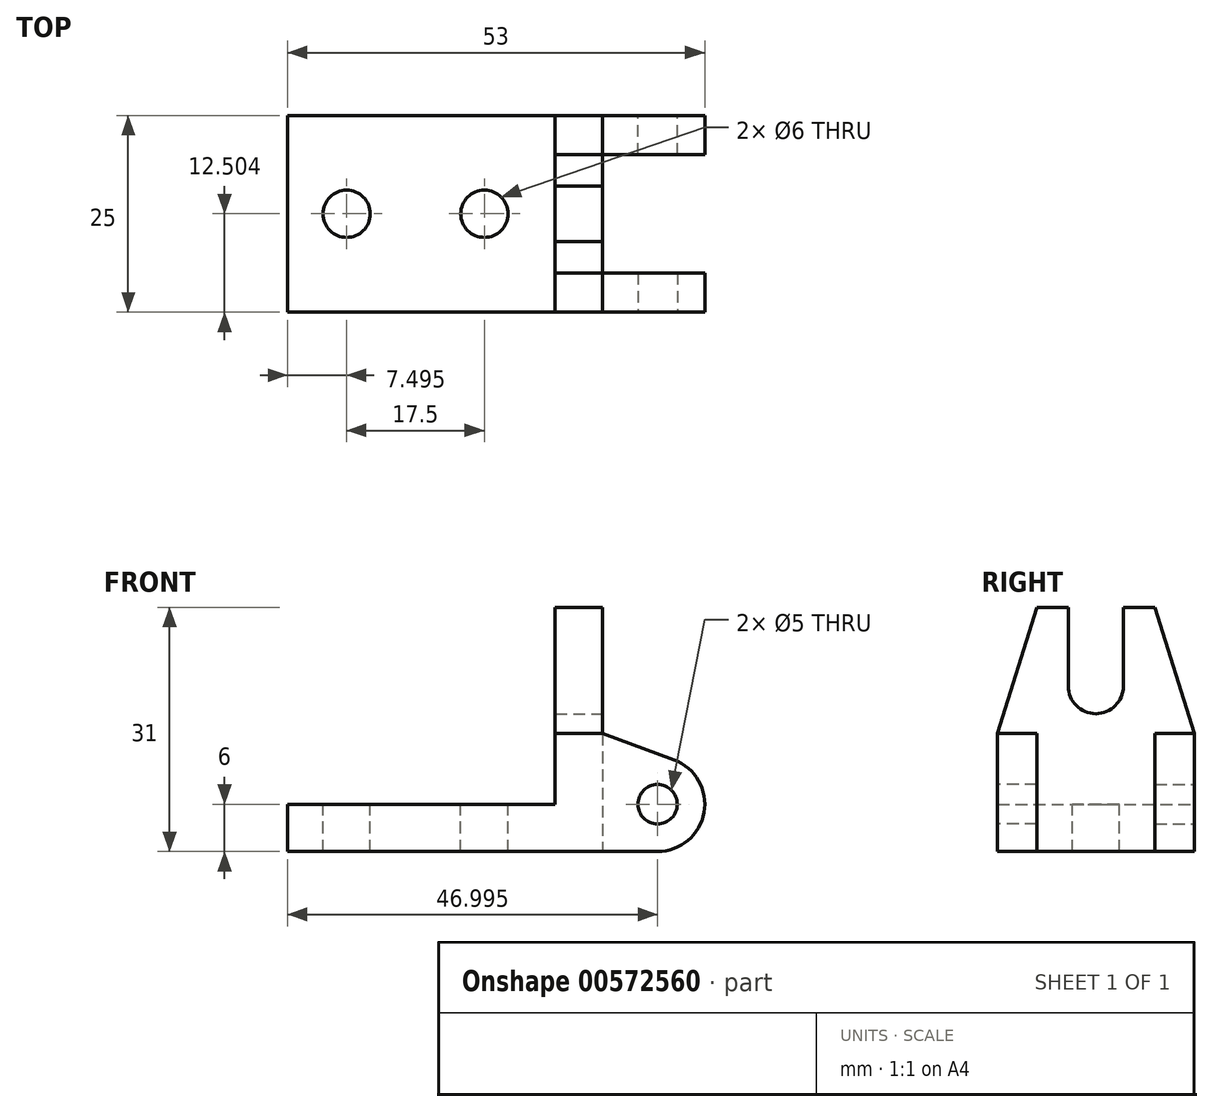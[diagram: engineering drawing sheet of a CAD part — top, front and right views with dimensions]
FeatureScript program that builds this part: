
annotation { "Feature Type Name" : "Feature", "Feature Type Description" : "" }
export const myFeature = defineFeature(function(context is Context, id is Id, definition is map)
    precondition{}
    {
        {
            var Q0;
            Q0=qCreatedBy(makeId("Top.planeOp"),FACE);
            var sketch = newSketch(context, id + "F0", { "sketchPlane" : qUnion([Q0])});
            skLineSegment(sketch, "E0.bottom", {"start": v(-32.98, -3.23) * mm, "end": v(7.02, -3.23) * mm});
            skLineSegment(sketch, "E0.top", {"start": v(-32.98, 21.77) * mm, "end": v(7.02, 21.77) * mm});
            skLineSegment(sketch, "E0.left", {"start": v(-32.98, -3.23) * mm, "end": v(-32.98, 21.77) * mm});
            skLineSegment(sketch, "E0.right", {"start": v(7.02, -3.23) * mm, "end": v(7.02, 21.77) * mm});
            skSolve(sketch);
        }
        {
            var Q0;
            Q0=makeQuery(id+"F0.imprint","IMPRINT",FACE,{"disambiguationData":[TD([[makeQuery(id+"F0.imprint","IMPRINT",EDGE,{"derivedFrom":sQuery(id+"F0.wireOp",EDGE,"E0.bottom")}),1.0]])]});
            extrude(context, id + "F1", {"entities" : qUnion([Q0]), "depth" : 6 * mm, "offsetDistance" : 25 * mm});
        }
        {
            var Q0;
            Q0=makeQuery(id+"F1.opExtrude","CAP_FACE",FACE,{"disambiguationData":[OSD([sQuery(id+"F0.wireOp",EDGE,"E0.bottom"),sQuery(id+"F0.wireOp",EDGE,"E0.top"),sQuery(id+"F0.wireOp",EDGE,"E0.left"),sQuery(id+"F0.wireOp",EDGE,"E0.right")])],"isStart":false});
            var sketch = newSketch(context, id + "F2", { "sketchPlane" : qUnion([Q0])});
            skLineSegment(sketch, "E1.bottom", {"start": v(7.02, -3.23) * mm, "end": v(1.02, -3.23) * mm});
            skLineSegment(sketch, "E1.top", {"start": v(7.02, 21.77) * mm, "end": v(1.02, 21.77) * mm});
            skLineSegment(sketch, "E1.left", {"start": v(7.02, -3.23) * mm, "end": v(7.02, 21.77) * mm});
            skLineSegment(sketch, "E1.right", {"start": v(1.02, -3.23) * mm, "end": v(1.02, 21.77) * mm});
            skSolve(sketch);
        }
        {
            var Q0;
            Q0=makeQuery(id+"F2.imprint","IMPRINT",FACE,{"disambiguationData":[TD([[makeQuery(id+"F2.imprint","IMPRINT",EDGE,{"derivedFrom":sQuery(id+"F2.wireOp",EDGE,"E1.bottom")}),1.0]])]});
            extrude(context, id + "F3", {"entities" : qUnion([Q0]), "operationType" : NewBodyOperationType.ADD, "depth" : 9 * mm, "offsetDistance" : 25 * mm});
        }
        {
            var Q0;
            Q0=makeQuery(id+"F3.boolean.opBoolean","MERGE",FACE,{"derivedFrom":[makeQuery(id+"F1.opExtrude","SWEPT_FACE",FACE,{"disambiguationData":[OSD([sQuery(id+"F0.wireOp",EDGE,"E0.right")])]}),makeQuery(id+"F3.opExtrude","SWEPT_FACE",FACE,{"disambiguationData":[OSD([sQuery(id+"F2.wireOp",EDGE,"E1.left")])]})]});
            var sketch = newSketch(context, id + "F4", { "sketchPlane" : qUnion([Q0])});
            skCircle(sketch, "E2", {"center": v(9.27, 21) * mm, "radius": 3.5 * mm});
            skPoint(sketch, "E2.centerSnap0", {"position": v(9.27, 15) * mm});
            skLineSegment(sketch, "E3.0.1", {"start": v(-3.23, 6) * mm, "end": v(21.77, 6) * mm});
            skLineSegment(sketch, "E3.0.3", {"start": v(21.77, 6) * mm, "end": v(-3.23, 6) * mm});
            skLineSegment(sketch, "E4", {"start": v(5.77, 21) * mm, "end": v(5.77, 31) * mm});
            skLineSegment(sketch, "E5", {"start": v(12.77, 21) * mm, "end": v(12.77, 31) * mm});
            skLineSegment(sketch, "E6", {"start": v(12.77, 31) * mm, "end": v(16.77, 31) * mm});
            skLineSegment(sketch, "E7", {"start": v(5.77, 31) * mm, "end": v(1.77, 31) * mm});
            skLineSegment(sketch, "E8", {"start": v(1.77, 31) * mm, "end": v(-3.23, 15) * mm});
            skLineSegment(sketch, "E9", {"start": v(16.77, 31) * mm, "end": v(21.77, 15) * mm});
            skSolve(sketch);
        }
        {
            var Q0;
            {var subQ1=sQuery(id+"F4.wireOp",EDGE,"E4");Q0=makeQuery(id+"F4.imprint","IMPRINT",FACE,{"disambiguationData":[TD([[makeQuery(id+"F4.imprint","IMPRINT",EDGE,{"derivedFrom":subQ1}),1.0]])]});}
            extrude(context, id + "F5", {"entities" : qUnion([Q0]), "operationType" : NewBodyOperationType.ADD, "oppositeDirection" : true, "depth" : 6 * mm, "offsetDistance" : 25 * mm});
        }
        {
            var Q0;
            Q0=makeQuery(id+"F3.boolean.opBoolean","MERGE",FACE,{"derivedFrom":[makeQuery(id+"F1.opExtrude","SWEPT_FACE",FACE,{"disambiguationData":[OSD([sQuery(id+"F0.wireOp",EDGE,"E0.bottom")])]}),makeQuery(id+"F3.opExtrude","SWEPT_FACE",FACE,{"disambiguationData":[OSD([sQuery(id+"F2.wireOp",EDGE,"E1.bottom")])]})]});
            var sketch = newSketch(context, id + "F6", { "sketchPlane" : qUnion([Q0])});
            skLineSegment(sketch, "E10", {"start": v(7.02, 0) * mm, "end": v(14.02, 0) * mm});
            skArc(sketch, "E11", {"start": v(14.02, 0) * mm, "mid": v(19.92, 4.94) * mm, "end": v(16.1, 11.62) * mm});
            skLineSegment(sketch, "E12", {"start": v(7.02, 15) * mm, "end": v(16.1, 11.62) * mm});
            skCircle(sketch, "E13", {"center": v(14.02, 6) * mm, "radius": 2.5 * mm});
            skSolve(sketch);
        }
        {
            var Q0;
            Q0=makeQuery(id+"F6.imprint","IMPRINT",FACE,{"disambiguationData":[TD([[makeQuery(id+"F6.imprint","IMPRINT",EDGE,{"derivedFrom":sQuery(id+"F6.wireOp",EDGE,"E10")}),1.0]])]});
            extrude(context, id + "F7", {"entities" : qUnion([Q0]), "operationType" : NewBodyOperationType.ADD, "oppositeDirection" : true, "depth" : 5 * mm, "offsetDistance" : 25 * mm});
        }
        {
            var Q0;
            Q0=makeQuery(id+"F3.boolean.opBoolean","MERGE",FACE,{"derivedFrom":[makeQuery(id+"F1.opExtrude","SWEPT_FACE",FACE,{"disambiguationData":[OSD([sQuery(id+"F0.wireOp",EDGE,"E0.top")])]}),makeQuery(id+"F3.opExtrude","SWEPT_FACE",FACE,{"disambiguationData":[OSD([sQuery(id+"F2.wireOp",EDGE,"E1.top")])]})]});
            var sketch = newSketch(context, id + "F8", { "sketchPlane" : qUnion([Q0])});
            skLineSegment(sketch, "E14.0.0", {"start": v(-7.02, 15) * mm, "end": v(-16.1, 11.62) * mm});
            skArc(sketch, "E14.0.1", {"start": v(-16.1, 11.62) * mm, "mid": v(-19.92, 4.94) * mm, "end": v(-14.02, 0) * mm});
            skLineSegment(sketch, "E14.0.2", {"start": v(-14.02, 0) * mm, "end": v(-7.02, 0) * mm});
            skLineSegment(sketch, "E14.0.3", {"start": v(-7.02, 0) * mm, "end": v(-7.02, 15) * mm});
            skCircle(sketch, "E15.0", {"center": v(-14.02, 6) * mm, "radius": 2.5 * mm});
            skSolve(sketch);
        }
        {
            var Q0;
            Q0=makeQuery(id+"F8.imprint","IMPRINT",FACE,{"disambiguationData":[TD([[makeQuery(id+"F8.imprint","IMPRINT",EDGE,{"derivedFrom":sQuery(id+"F8.wireOp",EDGE,"E14.0.0")}),1.0]])]});
            extrude(context, id + "F9", {"entities" : qUnion([Q0]), "operationType" : NewBodyOperationType.ADD, "oppositeDirection" : true, "depth" : 5 * mm, "offsetDistance" : 25 * mm});
        }
        {
            var Q0;
            Q0=makeQuery(id+"F1.opExtrude","CAP_FACE",FACE,{"disambiguationData":[OSD([sQuery(id+"F0.wireOp",EDGE,"E0.bottom"),sQuery(id+"F0.wireOp",EDGE,"E0.top"),sQuery(id+"F0.wireOp",EDGE,"E0.left"),sQuery(id+"F0.wireOp",EDGE,"E0.right")])],"isStart":false});
            var sketch = newSketch(context, id + "F10", { "sketchPlane" : qUnion([Q0])});
            skCircle(sketch, "E16", {"center": v(-25.48, 9.27) * mm, "radius": 3 * mm});
            skPoint(sketch, "E16.centerSnap0", {"position": v(-32.98, 9.27) * mm});
            skCircle(sketch, "E17", {"center": v(-7.98, 9.27) * mm, "radius": 3 * mm});
            skSolve(sketch);
        }
        {
            var Q0;
            Q0=makeQuery(id+"F10.imprint","IMPRINT",FACE,{"disambiguationData":[TD([[makeQuery(id+"F10.imprint","IMPRINT",EDGE,{"derivedFrom":sQuery(id+"F10.wireOp",EDGE,"E17")}),1.0]])]});
            var Q1;
            Q1=makeQuery(id+"F10.imprint","IMPRINT",FACE,{"disambiguationData":[TD([[makeQuery(id+"F10.imprint","IMPRINT",EDGE,{"derivedFrom":sQuery(id+"F10.wireOp",EDGE,"E16")}),1.0]])]});
            extrude(context, id + "F11", {"entities" : qUnion([Q0, Q1]), "operationType" : NewBodyOperationType.REMOVE, "endBound" : BoundingType.THROUGH_ALL, "oppositeDirection" : true, "depth" : 25 * mm, "offsetDistance" : 25 * mm});
        }
    });
